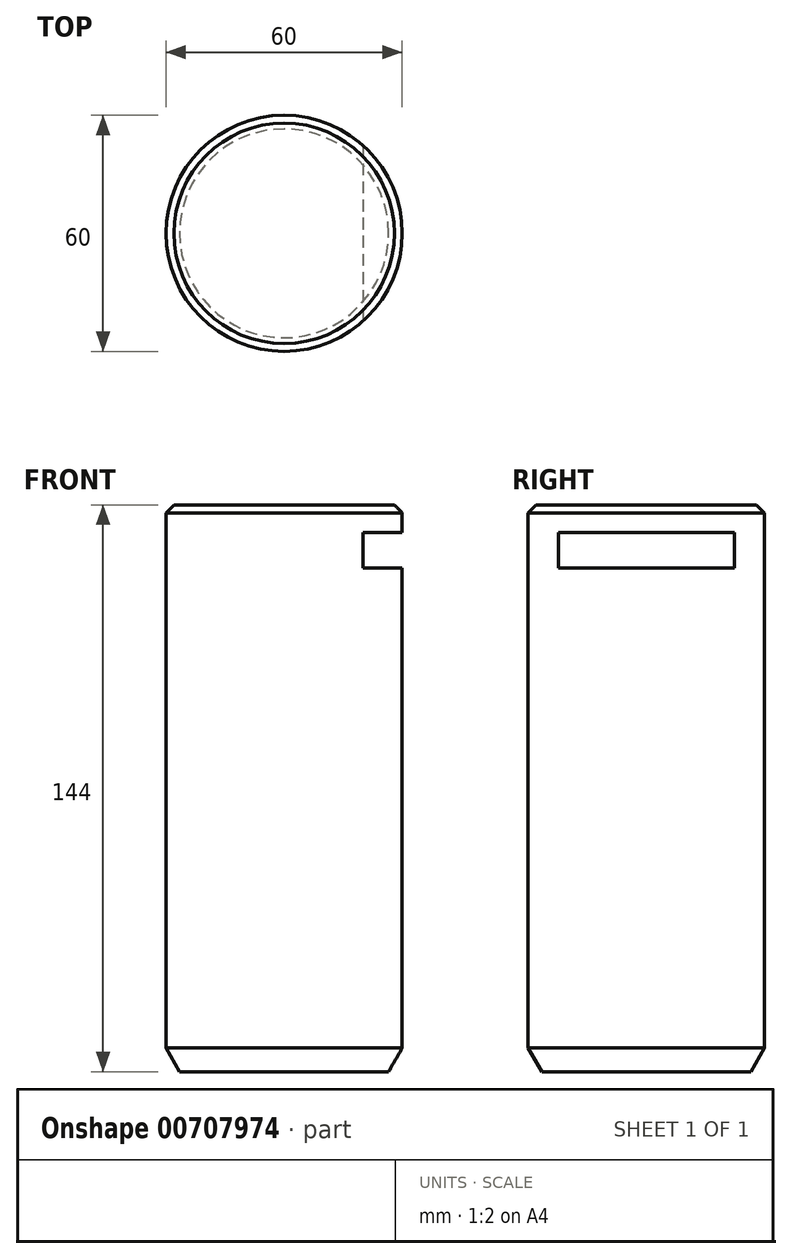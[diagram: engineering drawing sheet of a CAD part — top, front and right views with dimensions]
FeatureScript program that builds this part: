
annotation { "Feature Type Name" : "Feature", "Feature Type Description" : "" }
export const myFeature = defineFeature(function(context is Context, id is Id, definition is map)
    precondition{}
    {
        {
            var Q0;
            Q0=qCreatedBy(makeId("Top.planeOp"),FACE);
            var sketch = newSketch(context, id + "F0", { "sketchPlane" : qUnion([Q0])});
            skCircle(sketch, "E0", {"center": v(0, 0) * mm, "radius": 30 * mm});
            skSolve(sketch);
        }
        {
            var Q0;
            Q0=makeQuery(id+"F0.imprint","IMPRINT",FACE,{"disambiguationData":[TD([[makeQuery(id+"F0.imprint","IMPRINT",EDGE,{"derivedFrom":sQuery(id+"F0.wireOp",EDGE,"E0")}),1.0]])]});
            extrude(context, id + "F1", {"entities" : qUnion([Q0]), "endBound" : BoundingType.SYMMETRIC, "depth" : 144 * mm, "offsetDistance" : 25 * mm});
        }
        {
            var Q0;
            Q0=makeQuery(id+"F1.opExtrude","CAP_EDGE",EDGE,{"disambiguationData":[OSD([sQuery(id+"F0.wireOp",EDGE,"E0")])],"isStart":false});
            chamfer(context, id + "F2", {"entities" : qUnion([Q0]), "width" : 2 * mm, "tangentPropagation" : true});
        }
        {
            var Q0;
            Q0=makeQuery(id+"F1.opExtrude","CAP_EDGE",EDGE,{"disambiguationData":[OSD([sQuery(id+"F0.wireOp",EDGE,"E0")])],"isStart":true});
            chamfer(context, id + "F3", {"entities" : qUnion([Q0]), "chamferType" : ChamferType.OFFSET_ANGLE, "width" : 6 * mm, "oppositeDirection" : false, "angle" : 30 * degree, "tangentPropagation" : true});
        }
        {
            var Q0;
            Q0=qCreatedBy(makeId("Front.planeOp"),FACE);
            var sketch = newSketch(context, id + "F4", { "sketchPlane" : qUnion([Q0])});
            skLineSegment(sketch, "E1.bottom", {"start": v(20, 65) * mm, "end": v(35, 65) * mm});
            skLineSegment(sketch, "E1.top", {"start": v(20, 56) * mm, "end": v(35, 56) * mm});
            skLineSegment(sketch, "E1.left", {"start": v(20, 65) * mm, "end": v(20, 56) * mm});
            skLineSegment(sketch, "E1.right", {"start": v(35, 65) * mm, "end": v(35, 56) * mm});
            skSolve(sketch);
        }
        {
            var Q0;
            Q0=makeQuery(id+"F4.imprint","IMPRINT",FACE,{"disambiguationData":[TD([[makeQuery(id+"F4.imprint","IMPRINT",EDGE,{"derivedFrom":sQuery(id+"F4.wireOp",EDGE,"E1.bottom")}),-1.0]])]});
            extrude(context, id + "F5", {"entities" : qUnion([Q0]), "operationType" : NewBodyOperationType.REMOVE, "endBound" : BoundingType.SYMMETRIC, "oppositeDirection" : true, "depth" : 100 * mm, "offsetDistance" : 25 * mm});
        }
    });
